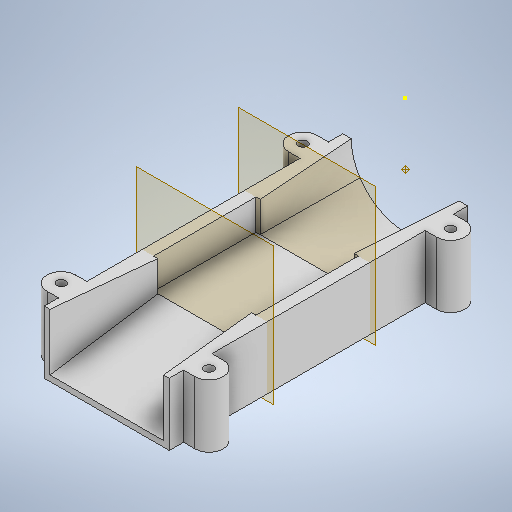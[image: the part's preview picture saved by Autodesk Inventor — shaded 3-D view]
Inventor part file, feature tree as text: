
AUTODESK INVENTOR PART (.ipt)
format: ipt  version: 2025.4 (Build 294407000, 407)  size: 395,264 bytes
history: native  units: mm
features: sketch x13, other x8, extrude x7, loft x2, hole x1
ambient origin geometry x8: Origin, YZ Plane, XZ Plane, XY Plane, X Axis, Y Axis, Z Axis, Center Point
bodies: Body1 (feature_tree)
feature tree (31):
  other  "Bryła1"
  other  "Płaszczyzna konstrukcyjna3"
  other  "Płaszczyzna konstrukcyjna4"
  other  "Płaszczyzna konstrukcyjna5"
  sketch  "Szkic7"
  sketch  "Szkic9"
  sketch  "Szkic10"
  sketch  "Szkic11"
  extrude  "Wyciągnięcie proste1"  Depth=35.0mm
  extrude  "Wyciągnięcie proste2"  Depth=38.0mm
  other  "Płaszczyzna konstrukcyjna6"
  other  "Płaszczyzna konstrukcyjna7"
  loft  "Wyciągnięcie złożone1"
  loft  "Wyciągnięcie złożone2"
  extrude  "Wyciągnięcie proste3"  Depth=40.0mm
  sketch  "Szkic14"
  extrude  "Wyciągnięcie proste4"  Depth=40.0mm
  extrude  "Wyciągnięcie proste5"  Depth=44.0mm
  sketch  "Szkic17"
  sketch  "Szkic18"
  extrude  "Wyciągnięcie proste6"  Depth=44.0mm
  hole  "Otwór1"  [1 undecoded]
  extrude  "Wyciągnięcie proste7"  Depth=35.5mm TaperAngle=0.0deg
  sketch  "Szkic12"
  other  "Krawędzie1"
  other  "Krawędzie2"
  sketch  "Szkic13"
  sketch  "Szkic15"
  sketch  "Szkic16"
  sketch  "Szkic19"
  sketch  "Szkic20"
note: 1 required parameter value undecoded (feature->parameter linkage not recoverable at this tier; creation-order binding heuristic only, values carry confidence <= 0.55)
